# Revit family: 4061106
name_source: partatom
category: Lighting Fixtures
revit_build: Autodesk Revit 2016 (Build: 20150220_1215(x64)
units: mm (PartAtom-declared; Revit-internal decimal feet)

## family parameters
Cut with Voids When Loaded = No
Host = Face
Light Source = Yes
OmniClass Number = 23.80.70.00
OmniClass Title = Lighting
Part Type = Normal
Room Calculation Point = No
Round Connector Dimension = Use Diameter
Shared = No

## types (1)
- 4061106 COLOSSAL 3400LM 830 DALI EM3 WHT
    Apparent Load = 30 VA
    Assembly Code = D5020200
    AssetType = Fixed
    ClassificationName = Uniclass2015
    ClassificationValue = EF_70_80
    Color Filter = 16777215
    Cost = 0 $
    Default Elevation = 1219 mm
    Description = Large 400 mm diameter circular architectural luminaire, can be surface mounted or suspended, aluminium housing with polycarbonate opal diffuser, 3400 lm, 30W, 113 lm/W, 3000K, CRI 80, 50,000 hours, IP40, IK03, Class 1, 220-240V, Energy class A++, DALI, Emergency 3 hours
    Dimming Lamp Color Temperature Shift = <None>
    DimmingControlOptions = Dimmable
    DocumentationLiterature = http://www.sylvania-lighting.com
    ElectricShockClassification = Class I
    Emit Shape Visible in Rendering = No
    Emit from Circle Diameter = 385 mm  [stored 1.26312 ft]
    IfcExportAs = IfcLightFixtureType
    IfcExportType = IfcLightFixtureType
    ImpactProtectionIndex = IK02
    IngressProtection = IP40
    InputNominalFrequency = 50/60 Hz
    InputVoltage = 230-240 V~
    Keynote = 16500
    Lamp = LED
    LampColourTemperature = 3000 K
    LampNominalLuminous = 3398 lm
    LampsType = LED
    Manufacturer = Feilo Sylvania
    ManufacturerName = Feilo Sylvania
    Material_1_SYL = Polycarbonate_Sylvania_Opal
    Material_2_SYL = Polycarbonate_Sylvania_White
    Material_3_SYL = LED-Sylvania
    Material_4_SYL = <By Category>
    Model = Colossal 3400lm 830 DALI EM3 WHT
    ModelNumber = 4061106
    ModelReference = Colossal 3400lm 830 DALI EM3 WHT
    Name = Colossal 3400lm 830 DALI EM3 WHT
    NominalDepth = 400 mm  [stored 1.31234 ft]
    NominalHeight = 87 mm
    NominalLength = 400 mm  [stored 1.31234 ft]
    Photometric Web File = 4061106.ies
    PowerConsumption = 30 W
    PowerFactor = 0
    Tilt Angle = -90.00°
    Type Image = <None>
    TypeName = Colossal 3400lm 830 DALI EM3 WHT
    URL = http://www.sylvania-lighting.com
    Voltage = 230 V

note: [stored X ft] marks values corroborated as IEEE doubles in the binary element streams (Revit-internal decimal feet)

## geometry (parser evidence)
native form markers: Sweep x3
no freeform markers — native parametric forms only
